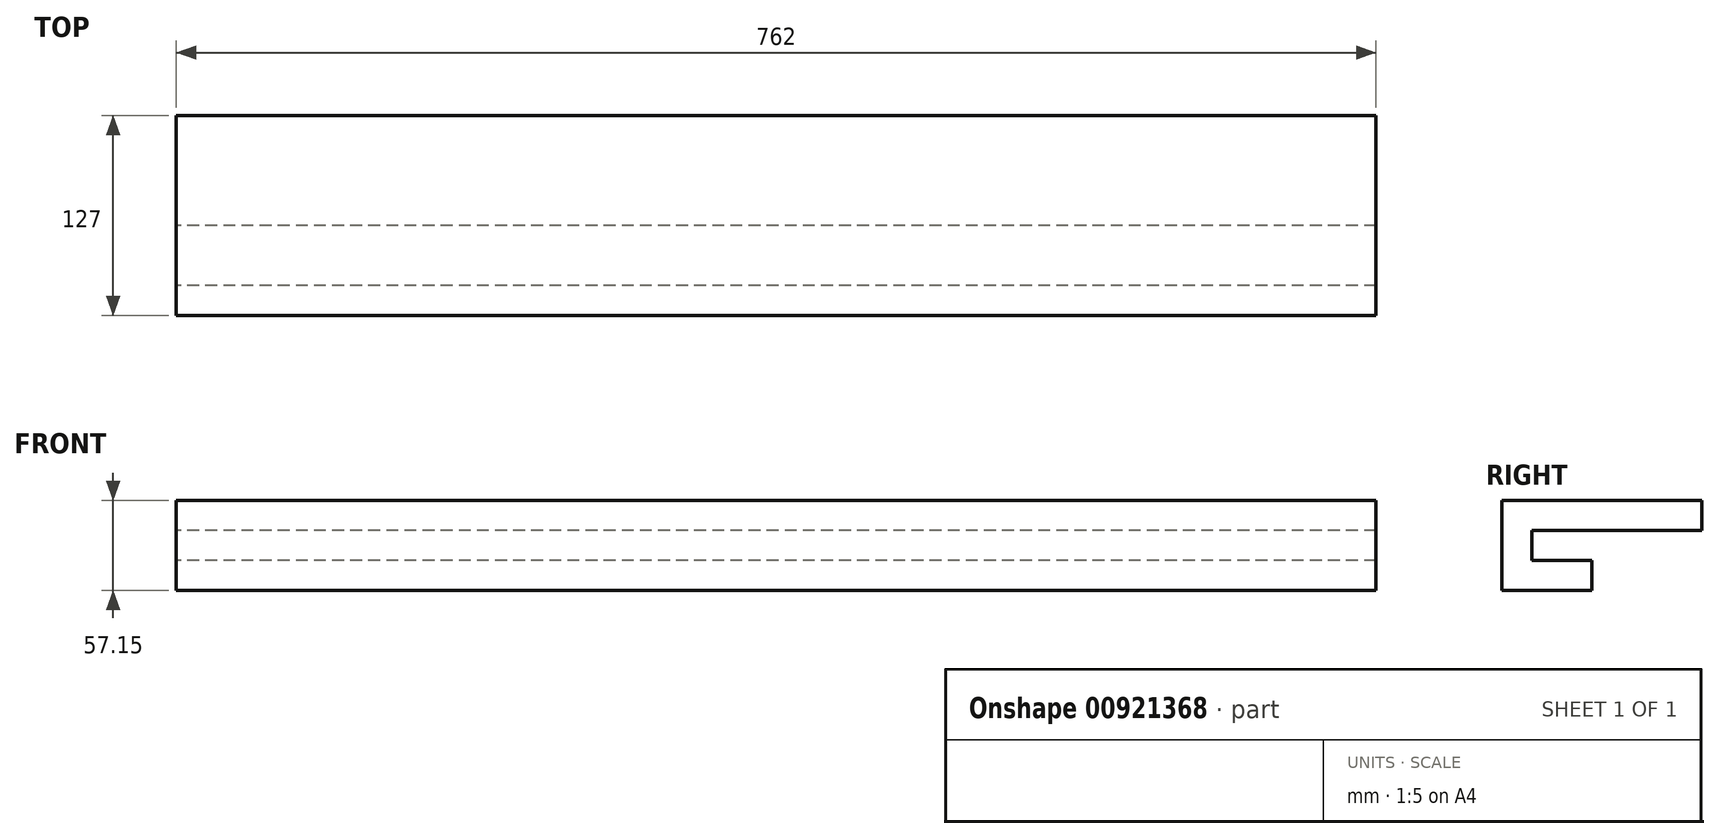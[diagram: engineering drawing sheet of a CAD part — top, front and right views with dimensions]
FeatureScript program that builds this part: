
annotation { "Feature Type Name" : "Feature", "Feature Type Description" : "" }
export const myFeature = defineFeature(function(context is Context, id is Id, definition is map)
    precondition{}
    {
        {
            var Q0;
            Q0=qCreatedBy(makeId("Right.planeOp"),FACE);
            var sketch = newSketch(context, id + "F0", { "sketchPlane" : qUnion([Q0])});
            skLineSegment(sketch, "E0", {"start": v(0, 0) * mm, "end": v(127, 0) * mm});
            skLineSegment(sketch, "E1", {"start": v(0, 0) * mm, "end": v(0, -57.15) * mm});
            skLineSegment(sketch, "E2", {"start": v(0, -57.15) * mm, "end": v(57.15, -57.15) * mm});
            skLineSegment(sketch, "E3", {"start": v(57.15, -57.15) * mm, "end": v(57.15, -38.1) * mm});
            skLineSegment(sketch, "E4", {"start": v(57.15, -38.1) * mm, "end": v(19.05, -38.1) * mm});
            skLineSegment(sketch, "E5", {"start": v(19.05, -38.1) * mm, "end": v(19.05, -19.05) * mm});
            skLineSegment(sketch, "E6", {"start": v(19.05, -19.05) * mm, "end": v(127, -19.05) * mm});
            skLineSegment(sketch, "E7", {"start": v(127, -19.05) * mm, "end": v(127, 0) * mm});
            skSolve(sketch);
        }
        {
            var Q0;
            Q0 = qSketchRegion(id + "F0", true);
            extrude(context, id + "F1", {"entities" : qUnion([Q0]), "endBound" : BoundingType.SYMMETRIC, "depth" : 762 * mm, "offsetDistance" : 25.4 * mm});
        }
    });
